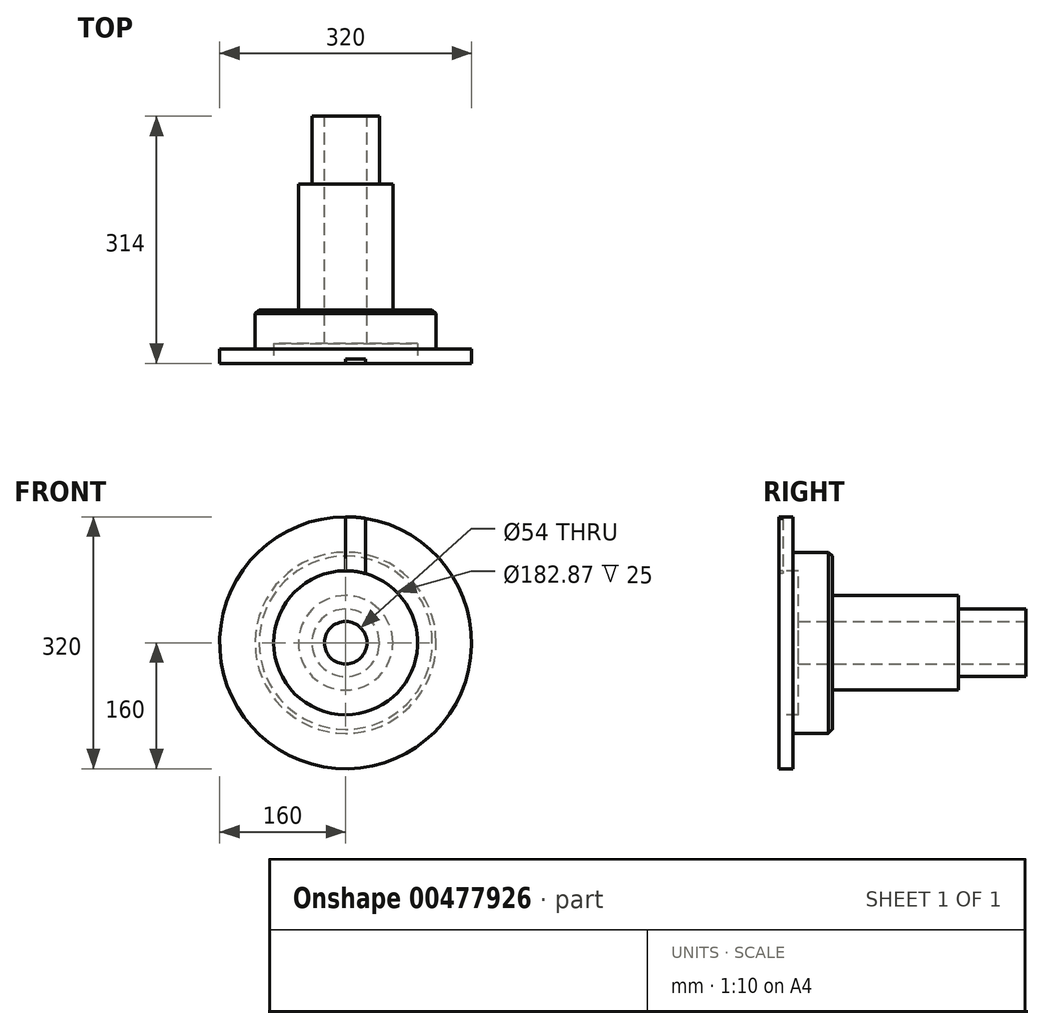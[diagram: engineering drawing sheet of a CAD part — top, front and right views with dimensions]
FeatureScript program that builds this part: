
annotation { "Feature Type Name" : "Feature", "Feature Type Description" : "" }
export const myFeature = defineFeature(function(context is Context, id is Id, definition is map)
    precondition{}
    {
        {
            var Q0;
            Q0=qCreatedBy(makeId("Front.planeOp"),FACE);
            var sketch = newSketch(context, id + "F0", { "sketchPlane" : qUnion([Q0])});
            skCircle(sketch, "E0", {"center": v(0, 0) * mm, "radius": 60 * mm});
            skSolve(sketch);
        }
        {
            var Q0;
            Q0=qSketchRegion(id+"F0",true);
            extrude(context, id + "F1", {"entities" : qUnion([Q0]), "depth" : 160 * mm});
        }
        {
            var Q0;
            Q0=makeQuery(id+"F1.opExtrude","CAP_FACE",FACE,{"disambiguationData":[OSD([sQuery(id+"F0.wireOp",EDGE,"E0")])],"isStart":false});
            var sketch = newSketch(context, id + "F2", { "sketchPlane" : qUnion([Q0])});
            skCircle(sketch, "E1", {"center": v(0, 0) * mm, "radius": 115 * mm});
            skSolve(sketch);
        }
        {
            var Q0;
            Q0=qSketchRegion(id+"F2",true);
            extrude(context, id + "F3", {"entities" : qUnion([Q0]), "operationType" : NewBodyOperationType.ADD, "depth" : 50 * mm});
        }
        {
            var Q0;
            Q0=makeQuery(id+"F3.opExtrude","CAP_FACE",FACE,{"disambiguationData":[OSD([sQuery(id+"F2.wireOp",EDGE,"E1")])],"isStart":false});
            var sketch = newSketch(context, id + "F4", { "sketchPlane" : qUnion([Q0])});
            skCircle(sketch, "E2", {"center": v(0, 0) * mm, "radius": 160 * mm});
            skSolve(sketch);
        }
        {
            var Q0;
            Q0=qSketchRegion(id+"F4",true);
            extrude(context, id + "F5", {"entities" : qUnion([Q0]), "operationType" : NewBodyOperationType.ADD, "depth" : 18 * mm});
        }
        {
            var Q0;
            Q0=makeQuery(id+"F3.opExtrude","CAP_EDGE",EDGE,{"disambiguationData":[OSD([sQuery(id+"F2.wireOp",EDGE,"E1")])],"isStart":true});
            chamfer(context, id + "F6", {"entities" : qUnion([Q0]), "width" : 5 * mm, "tangentPropagation" : true});
        }
        {
            var Q0;
            Q0=makeQuery(id+"F1.opExtrude","CAP_FACE",FACE,{"disambiguationData":[OSD([sQuery(id+"F0.wireOp",EDGE,"E0")])],"isStart":true});
            var sketch = newSketch(context, id + "F7", { "sketchPlane" : qUnion([Q0])});
            skCircle(sketch, "E3", {"center": v(0, 0) * mm, "radius": 42.88 * mm});
            skSolve(sketch);
        }
        {
            var Q0;
            Q0=qSketchRegion(id+"F7",true);
            extrude(context, id + "F8", {"entities" : qUnion([Q0]), "operationType" : NewBodyOperationType.ADD, "depth" : 86 * mm});
        }
        {
            var Q0;
            Q0=makeQuery(id+"F8.opExtrude","CAP_FACE",FACE,{"disambiguationData":[OSD([sQuery(id+"F7.wireOp",EDGE,"E3")])],"isStart":false});
            var sketch = newSketch(context, id + "F9", { "sketchPlane" : qUnion([Q0])});
            skCircle(sketch, "E4", {"center": v(0, 0) * mm, "radius": 27 * mm});
            skSolve(sketch);
        }
        {
            var Q0;
            Q0=qSketchRegion(id+"F9",true);
            extrude(context, id + "F10", {"entities" : qUnion([Q0]), "operationType" : NewBodyOperationType.REMOVE, "oppositeDirection" : true, "depth" : 430 * mm});
        }
        {
            var Q0;
            Q0=makeQuery(id+"F5.opExtrude","CAP_FACE",FACE,{"disambiguationData":[OSD([sQuery(id+"F4.wireOp",EDGE,"E2")])],"isStart":false});
            var sketch = newSketch(context, id + "F11", { "sketchPlane" : qUnion([Q0])});
            skCircle(sketch, "E5", {"center": v(0, 0) * mm, "radius": 91.44 * mm});
            skSolve(sketch);
        }
        {
            var Q0;
            Q0=qSketchRegion(id+"F11",true);
            extrude(context, id + "F12", {"entities" : qUnion([Q0]), "operationType" : NewBodyOperationType.REMOVE, "oppositeDirection" : true, "depth" : 25 * mm});
        }
        {
            var Q0;
            Q0=qCreatedBy(makeId("Right.planeOp"),FACE);
            var sketch = newSketch(context, id + "F13", { "sketchPlane" : qUnion([Q0])});
            skLineSegment(sketch, "E6.bottom", {"start": v(-238.94, 166.46) * mm, "end": v(-222.48, 166.46) * mm});
            skLineSegment(sketch, "E6.top", {"start": v(-238.94, 63.93) * mm, "end": v(-222.48, 63.93) * mm});
            skLineSegment(sketch, "E6.left", {"start": v(-238.94, 166.46) * mm, "end": v(-238.94, 63.93) * mm});
            skLineSegment(sketch, "E6.right", {"start": v(-222.48, 166.46) * mm, "end": v(-222.48, 63.93) * mm});
            skSolve(sketch);
        }
        {
            var Q0;
            Q0 = qSketchRegion(id + "F13", true);
            extrude(context, id + "F14", {"entities" : qUnion([Q0]), "operationType" : NewBodyOperationType.REMOVE, "depth" : 25 * mm});
        }
    });
